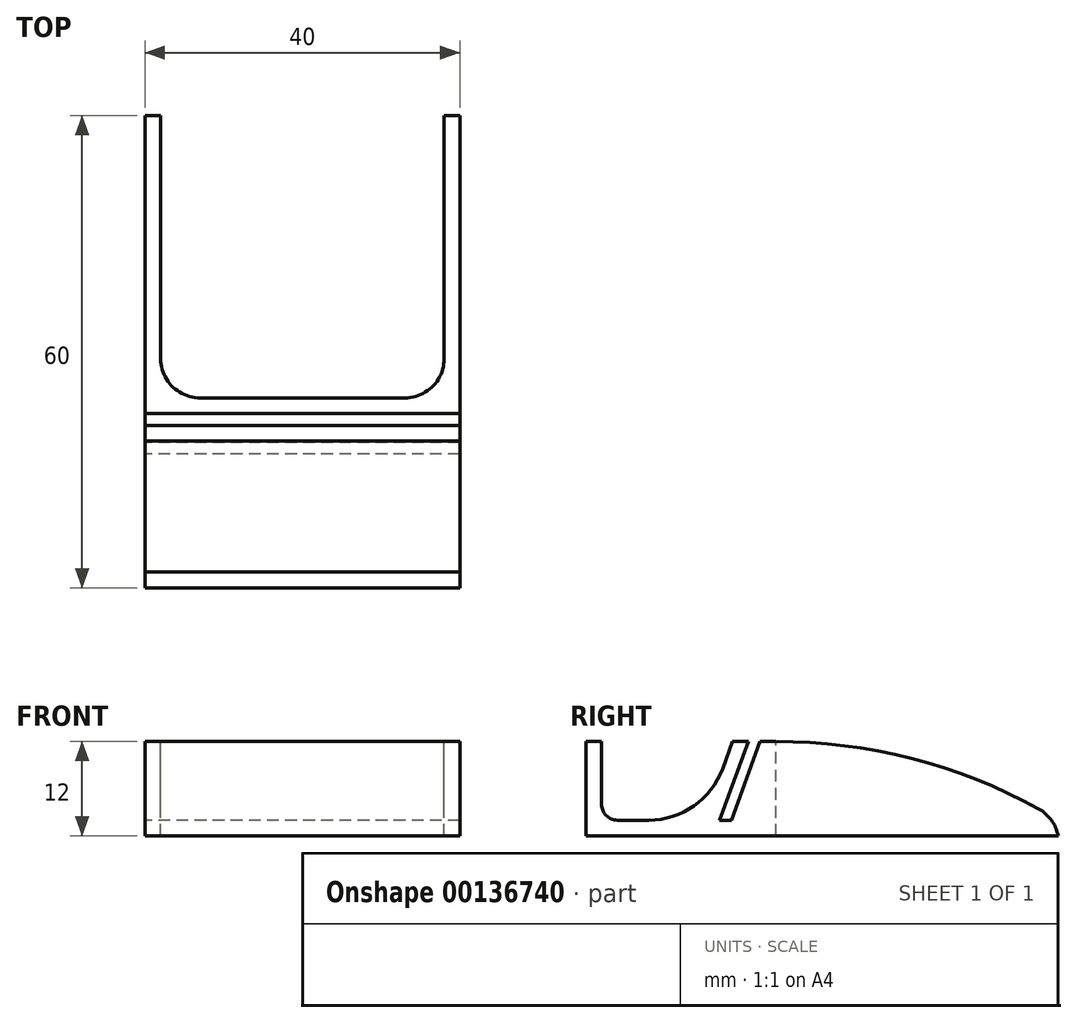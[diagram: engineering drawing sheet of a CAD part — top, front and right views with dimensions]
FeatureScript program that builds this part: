
annotation { "Feature Type Name" : "Feature", "Feature Type Description" : "" }
export const myFeature = defineFeature(function(context is Context, id is Id, definition is map)
    precondition{}
    {
        {
            var Q0;
            Q0=qCreatedBy(makeId("Right.planeOp"),FACE);
            var sketch = newSketch(context, id + "F0", { "sketchPlane" : qUnion([Q0])});
            skLineSegment(sketch, "E0", {"start": v(0, 0) * mm, "end": v(13, 0) * mm});
            skLineSegment(sketch, "E1", {"start": v(13, 0) * mm, "end": v(16.64, 10) * mm});
            skLineSegment(sketch, "E2", {"start": v(16.64, 10) * mm, "end": v(18.64, 10) * mm});
            skLineSegment(sketch, "E3", {"start": v(18.64, 10) * mm, "end": v(15, 0) * mm});
            skLineSegment(sketch, "E4", {"start": v(15, 0) * mm, "end": v(16.49, 0) * mm});
            skLineSegment(sketch, "E5", {"start": v(16.49, 0) * mm, "end": v(20.13, 10) * mm});
            skLineSegment(sketch, "E6", {"start": v(20.13, 10) * mm, "end": v(22.13, 10) * mm});
            skLineSegment(sketch, "E7", {"start": v(22.13, 10) * mm, "end": v(22.13, 0) * mm});
            skLineSegment(sketch, "E8", {"start": v(22.13, 0) * mm, "end": v(58, 0) * mm});
            skLineSegment(sketch, "E9", {"start": v(58, 0) * mm, "end": v(58, -2) * mm});
            skLineSegment(sketch, "E10", {"start": v(58, -2) * mm, "end": v(-2, -2) * mm});
            skLineSegment(sketch, "E11", {"start": v(-2, -2) * mm, "end": v(-2, 10) * mm});
            skLineSegment(sketch, "E12", {"start": v(-2, 10) * mm, "end": v(0, 10) * mm});
            skLineSegment(sketch, "E13", {"start": v(0, 10) * mm, "end": v(0, 0) * mm});
            skArc(sketch, "E14", {"start": v(58, 0) * mm, "mid": v(40.75, 7.45) * mm, "end": v(22.13, 10) * mm});
            skSolve(sketch);
        }
        {
            var Q0;
            Q0=makeQuery(id+"F0.imprint","IMPRINT",FACE,{"disambiguationData":[TD([[makeQuery(id+"F0.imprint","IMPRINT",EDGE,{"derivedFrom":sQuery(id+"F0.wireOp",EDGE,"E0")}),-1.0]])]});
            var Q1;
            Q1=makeQuery(id+"F0.imprint","IMPRINT",FACE,{"disambiguationData":[TD([[makeQuery(id+"F0.imprint","IMPRINT",EDGE,{"derivedFrom":sQuery(id+"F0.wireOp",EDGE,"E7")}),1.0]])]});
            extrude(context, id + "F1", {"entities" : qUnion([Q0, Q1]), "depth" : 40 * mm});
        }
        {
            var Q0;
            Q0=makeQuery(id+"F1.opExtrude","SWEPT_EDGE",EDGE,{"disambiguationData":[OSD([sQuery(id+"F0.wireOp",EDGE,"E0"),sQuery(id+"F0.wireOp",EDGE,"E1")])]});
            fillet(context, id + "F2", {"entities" : qUnion([Q0]), "radius" : 10 * mm, "tangentPropagation" : true, "allowEdgeOverflow" : false});
        }
        {
            var Q0;
            Q0=makeQuery(id+"F1.opExtrude","SWEPT_EDGE",EDGE,{"disambiguationData":[OSD([sQuery(id+"F0.wireOp",EDGE,"E0"),sQuery(id+"F0.wireOp",EDGE,"E13")])]});
            fillet(context, id + "F3", {"entities" : qUnion([Q0]), "radius" : 2 * mm, "tangentPropagation" : true, "allowEdgeOverflow" : false});
        }
        {
            var Q0;
            Q0=makeQuery(id+"F1.opExtrude","SWEPT_FACE",FACE,{"disambiguationData":[OSD([sQuery(id+"F0.wireOp",EDGE,"E6")])]});
            var sketch = newSketch(context, id + "F4", { "sketchPlane" : qUnion([Q0])});
            skLineSegment(sketch, "E15.bottom", {"start": v(2, 22.13) * mm, "end": v(38, 22.13) * mm});
            skLineSegment(sketch, "E15.top", {"start": v(2, 58) * mm, "end": v(38, 58) * mm});
            skLineSegment(sketch, "E15.left", {"start": v(2, 22.13) * mm, "end": v(2, 58) * mm});
            skLineSegment(sketch, "E15.right", {"start": v(38, 22.13) * mm, "end": v(38, 58) * mm});
            skSolve(sketch);
        }
        {
            var Q0;
            Q0=makeQuery(id+"F4.imprint","IMPRINT",FACE,{"disambiguationData":[TD([[makeQuery(id+"F4.imprint","IMPRINT",EDGE,{"derivedFrom":sQuery(id+"F4.wireOp",EDGE,"E15.bottom")}),-1.0]])]});
            extrude(context, id + "F5", {"entities" : qUnion([Q0]), "operationType" : NewBodyOperationType.REMOVE, "oppositeDirection" : true, "depth" : 25 * mm});
        }
        {
            var Q0;
            Q0=makeQuery(id+"F5.boolean.opBoolean","COPY",EDGE,{"derivedFrom":makeQuery(id+"F5.opExtrude","SWEPT_EDGE",EDGE,{"disambiguationData":[OSD([sQuery(id+"F0.wireOp",EDGE,"E6"),sQuery(id+"F0.wireOp",EDGE,"E7"),sQuery(id+"F0.wireOp",EDGE,"E14"),sQuery(id+"F4.wireOp",EDGE,"E15.bottom"),sQuery(id+"F4.wireOp",EDGE,"E15.left")])]})});
            var Q1;
            Q1=makeQuery(id+"F5.boolean.opBoolean","COPY",EDGE,{"derivedFrom":makeQuery(id+"F5.opExtrude","SWEPT_EDGE",EDGE,{"disambiguationData":[OSD([sQuery(id+"F0.wireOp",EDGE,"E6"),sQuery(id+"F0.wireOp",EDGE,"E7"),sQuery(id+"F0.wireOp",EDGE,"E14"),sQuery(id+"F4.wireOp",EDGE,"E15.bottom"),sQuery(id+"F4.wireOp",EDGE,"E15.right")])]})});
            fillet(context, id + "F6", {"entities" : qUnion([Q0, Q1]), "radius" : 5 * mm, "tangentPropagation" : true, "allowEdgeOverflow" : false});
        }
        {
            var Q0;
            {var subQ0=sQuery(id+"F0.wireOp",EDGE,"E14");var subQ1=sQuery(id+"F0.wireOp",EDGE,"E9");Q0=makeQuery(id+"F5.boolean.opBoolean","SPLIT",EDGE,{"disambiguationData":[TD([makeQuery(id+"F5.opExtrude","SWEPT_FACE",FACE,{"disambiguationData":[OSD([sQuery(id+"F4.wireOp",EDGE,"E15.left")])]})])],"derivedFrom":makeQuery(id+"F1.opExtrude","SWEPT_EDGE",EDGE,{"disambiguationData":[OSD([sQuery(id+"F0.wireOp",EDGE,"E8"),subQ1,subQ0])]})});}
            var Q1;
            {var subQ0=sQuery(id+"F0.wireOp",EDGE,"E14");var subQ1=sQuery(id+"F0.wireOp",EDGE,"E9");Q1=makeQuery(id+"F5.boolean.opBoolean","SPLIT",EDGE,{"disambiguationData":[TD([makeQuery(id+"F5.opExtrude","SWEPT_FACE",FACE,{"disambiguationData":[OSD([sQuery(id+"F4.wireOp",EDGE,"E15.right")])]})])],"derivedFrom":makeQuery(id+"F1.opExtrude","SWEPT_EDGE",EDGE,{"disambiguationData":[OSD([sQuery(id+"F0.wireOp",EDGE,"E8"),subQ1,subQ0])]})});}
            fillet(context, id + "F7", {"entities" : qUnion([Q0, Q1]), "radius" : 5 * mm, "tangentPropagation" : true, "allowEdgeOverflow" : false});
        }
    });
